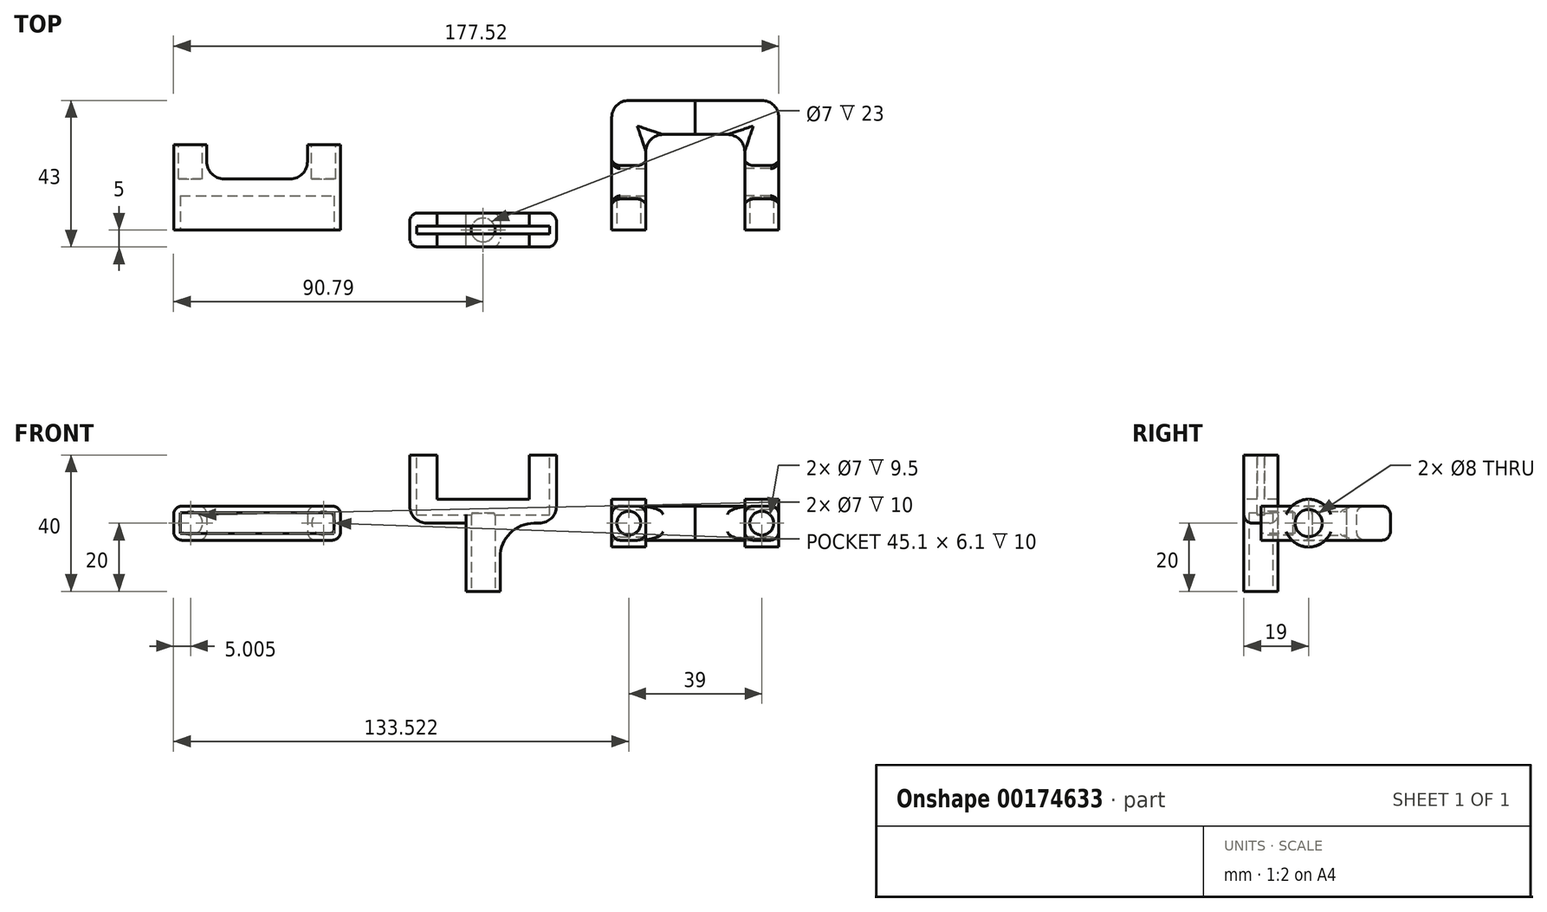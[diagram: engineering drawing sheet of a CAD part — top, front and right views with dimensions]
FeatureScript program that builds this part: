
annotation { "Feature Type Name" : "Feature", "Feature Type Description" : "" }
export const myFeature = defineFeature(function(context is Context, id is Id, definition is map)
    precondition{}
    {
        {
            var Q0;
            Q0=qCreatedBy(makeId("Top.planeOp"),FACE);
            var sketch = newSketch(context, id + "F0", { "sketchPlane" : qUnion([Q0])});
            skLineSegment(sketch, "E0.bottom", {"start": v(21.5, 5) * mm, "end": v(-21.5, 5) * mm});
            skLineSegment(sketch, "E0.top", {"start": v(21.5, -5) * mm, "end": v(-21.5, -5) * mm});
            skLineSegment(sketch, "E0.left", {"start": v(21.5, 5) * mm, "end": v(21.5, -5) * mm});
            skLineSegment(sketch, "E0.right", {"start": v(-21.5, 5) * mm, "end": v(-21.5, -5) * mm});
            skPoint(sketch, "E0.middle", {"position": v(0, 0) * mm});
            skSolve(sketch);
        }
        {
            var Q0;
            Q0=qSketchRegion(id+"F0",true);
            extrude(context, id + "F1", {"entities" : qUnion([Q0]), "depth" : 7 * mm});
        }
        {
            var Q0;
            Q0=makeQuery(id+"F1.opExtrude","CAP_FACE",FACE,{"disambiguationData":[OSD([sQuery(id+"F0.wireOp",EDGE,"E0.bottom"),sQuery(id+"F0.wireOp",EDGE,"E0.top"),sQuery(id+"F0.wireOp",EDGE,"E0.left"),sQuery(id+"F0.wireOp",EDGE,"E0.right")])],"isStart":false});
            var sketch = newSketch(context, id + "F2", { "sketchPlane" : qUnion([Q0])});
            skLineSegment(sketch, "E1.bottom", {"start": v(-21.5, 5) * mm, "end": v(-13.5, 5) * mm});
            skLineSegment(sketch, "E1.top", {"start": v(-21.5, -5) * mm, "end": v(-13.5, -5) * mm});
            skLineSegment(sketch, "E1.left", {"start": v(-21.5, 5) * mm, "end": v(-21.5, -5) * mm});
            skLineSegment(sketch, "E1.right", {"start": v(-13.5, 5) * mm, "end": v(-13.5, -5) * mm});
            skLineSegment(sketch, "E2.bottom", {"start": v(21.5, 5) * mm, "end": v(13.5, 5) * mm});
            skLineSegment(sketch, "E2.top", {"start": v(21.5, -5) * mm, "end": v(13.5, -5) * mm});
            skLineSegment(sketch, "E2.left", {"start": v(21.5, 5) * mm, "end": v(21.5, -5) * mm});
            skLineSegment(sketch, "E2.right", {"start": v(13.5, 5) * mm, "end": v(13.5, -5) * mm});
            skSolve(sketch);
        }
        {
            var Q0;
            Q0=makeQuery(id+"F2.imprint","IMPRINT",FACE,{"disambiguationData":[TD([[makeQuery(id+"F2.imprint","IMPRINT",EDGE,{"derivedFrom":sQuery(id+"F2.wireOp",EDGE,"E1.bottom")}),1.0]])]});
            var Q1;
            Q1=makeQuery(id+"F2.imprint","IMPRINT",FACE,{"disambiguationData":[TD([[makeQuery(id+"F2.imprint","IMPRINT",EDGE,{"derivedFrom":sQuery(id+"F2.wireOp",EDGE,"E2.bottom")}),1.0]])]});
            extrude(context, id + "F3", {"entities" : qUnion([Q0, Q1]), "operationType" : NewBodyOperationType.ADD, "depth" : 13 * mm});
        }
        {
            var Q0;
            Q0=makeQuery(id+"F1.opExtrude","CAP_FACE",FACE,{"disambiguationData":[OSD([sQuery(id+"F0.wireOp",EDGE,"E0.bottom"),sQuery(id+"F0.wireOp",EDGE,"E0.top"),sQuery(id+"F0.wireOp",EDGE,"E0.left"),sQuery(id+"F0.wireOp",EDGE,"E0.right")])],"isStart":true});
            var sketch = newSketch(context, id + "F4", { "sketchPlane" : qUnion([Q0])});
            skLineSegment(sketch, "E3.bottom", {"start": v(-5, 5) * mm, "end": v(5, 5) * mm});
            skLineSegment(sketch, "E3.top", {"start": v(-5, -5) * mm, "end": v(5, -5) * mm});
            skLineSegment(sketch, "E3.left", {"start": v(-5, 5) * mm, "end": v(-5, -5) * mm});
            skLineSegment(sketch, "E3.right", {"start": v(5, 5) * mm, "end": v(5, -5) * mm});
            skPoint(sketch, "E3.middle", {"position": v(0, 0) * mm});
            skSolve(sketch);
        }
        {
            var Q0;
            Q0=makeQuery(id+"F4.imprint","IMPRINT",FACE,{"disambiguationData":[TD([[makeQuery(id+"F4.imprint","IMPRINT",EDGE,{"derivedFrom":sQuery(id+"F4.wireOp",EDGE,"E3.bottom")}),1.0]])]});
            extrude(context, id + "F5", {"entities" : qUnion([Q0]), "operationType" : NewBodyOperationType.ADD, "depth" : 20 * mm});
        }
        {
            var Q0;
            Q0=makeQuery(id+"F5.opExtrude","CAP_FACE",FACE,{"disambiguationData":[OSD([sQuery(id+"F4.wireOp",EDGE,"E3.bottom"),sQuery(id+"F4.wireOp",EDGE,"E3.top"),sQuery(id+"F4.wireOp",EDGE,"E3.left"),sQuery(id+"F4.wireOp",EDGE,"E3.right")])],"isStart":false});
            var sketch = newSketch(context, id + "F6", { "sketchPlane" : qUnion([Q0])});
            skCircle(sketch, "E4", {"center": v(0, 0) * mm, "radius": 3.5 * mm});
            skSolve(sketch);
        }
        {
            var Q0;
            Q0=qSketchRegion(id+"F6",true);
            extrude(context, id + "F7", {"entities" : qUnion([Q0]), "operationType" : NewBodyOperationType.REMOVE, "oppositeDirection" : true, "depth" : 23 * mm});
        }
        {
            var Q0;
            Q0=makeQuery(id+"F5.boolean.opBoolean","MERGE",FACE,{"derivedFrom":[makeQuery(id+"F3.boolean.opBoolean","MERGE",FACE,{"derivedFrom":[makeQuery(id+"F1.opExtrude","SWEPT_FACE",FACE,{"disambiguationData":[OSD([sQuery(id+"F0.wireOp",EDGE,"E0.top")])]}),makeQuery(id+"F3.opExtrude","SWEPT_FACE",FACE,{"disambiguationData":[OSD([sQuery(id+"F2.wireOp",EDGE,"E1.top")])]}),makeQuery(id+"F3.opExtrude","SWEPT_FACE",FACE,{"disambiguationData":[OSD([sQuery(id+"F2.wireOp",EDGE,"E2.top")])]})]}),makeQuery(id+"F5.opExtrude","SWEPT_FACE",FACE,{"disambiguationData":[OSD([sQuery(id+"F4.wireOp",EDGE,"E3.bottom")])]})]});
            var sketch = newSketch(context, id + "F8", { "sketchPlane" : qUnion([Q0])});
            skLineSegment(sketch, "E5", {"start": v(-5, 0) * mm, "end": v(-15, 0) * mm});
            skLineSegment(sketch, "E6", {"start": v(-15, 0) * mm, "end": v(-5, 0) * mm});
            skLineSegment(sketch, "E7", {"start": v(-5, 0) * mm, "end": v(-5, -10) * mm});
            skArc(sketch, "E8", {"start": v(-5, -10) * mm, "mid": v(-7.93, -2.93) * mm, "end": v(-15, 0) * mm});
            skLineSegment(sketch, "E9", {"start": v(5, 0) * mm, "end": v(15, 0) * mm});
            skLineSegment(sketch, "E10", {"start": v(5, 0) * mm, "end": v(5, -10) * mm});
            skArc(sketch, "E11", {"start": v(15, 0) * mm, "mid": v(7.93, -2.93) * mm, "end": v(5, -10) * mm});
            skSolve(sketch);
        }
        {
            var Q0;
            Q0=makeQuery(id+"F8.imprint","IMPRINT",FACE,{"disambiguationData":[TD([[makeQuery(id+"F8.imprint","IMPRINT",EDGE,{"derivedFrom":sQuery(id+"F8.wireOp",EDGE,"E6")}),1.0]])]});
            var Q1;
            Q1=makeQuery(id+"F8.imprint","IMPRINT",FACE,{"disambiguationData":[TD([[makeQuery(id+"F8.imprint","IMPRINT",EDGE,{"derivedFrom":sQuery(id+"F8.wireOp",EDGE,"E9")}),1.0]])]});
            extrude(context, id + "F9", {"entities" : qUnion([Q0, Q1]), "operationType" : NewBodyOperationType.ADD, "oppositeDirection" : true, "depth" : 10 * mm});
        }
        {
            var Q0;
            Q0=makeQuery(id+"F3.opExtrude","CAP_FACE",FACE,{"disambiguationData":[OSD([sQuery(id+"F2.wireOp",EDGE,"E1.bottom"),sQuery(id+"F2.wireOp",EDGE,"E1.top"),sQuery(id+"F2.wireOp",EDGE,"E1.left"),sQuery(id+"F2.wireOp",EDGE,"E1.right")])],"isStart":false});
            var sketch = newSketch(context, id + "F10", { "sketchPlane" : qUnion([Q0])});
            skLineSegment(sketch, "E12.bottom", {"start": v(-19.5, 1.13) * mm, "end": v(19.5, 1.13) * mm});
            skLineSegment(sketch, "E12.top", {"start": v(-19.5, -1.13) * mm, "end": v(19.5, -1.13) * mm});
            skLineSegment(sketch, "E12.left", {"start": v(-19.5, 1.13) * mm, "end": v(-19.5, -1.13) * mm});
            skLineSegment(sketch, "E12.right", {"start": v(19.5, 1.13) * mm, "end": v(19.5, -1.13) * mm});
            skPoint(sketch, "E12.middle", {"position": v(0, 0) * mm});
            skSolve(sketch);
        }
        {
            var Q0;
            Q0=qSketchRegion(id+"F10",true);
            extrude(context, id + "F11", {"entities" : qUnion([Q0]), "oppositeDirection" : true, "depth" : 17.6 * mm});
        }
        {
            var Q0;
            Q0=makeQuery(id+"F11.opExtrude","SWEPT_BODY",BODY,{"disambiguationData":[OSD([sQuery(id+"F10.wireOp",EDGE,"E12.bottom"),sQuery(id+"F10.wireOp",EDGE,"E12.top"),sQuery(id+"F10.wireOp",EDGE,"E12.left"),sQuery(id+"F10.wireOp",EDGE,"E12.right")])]});
            var Q1;
            Q1=makeQuery(id+"F1.opExtrude","SWEPT_BODY",BODY,{"disambiguationData":[OSD([sQuery(id+"F0.wireOp",EDGE,"E0.bottom"),sQuery(id+"F0.wireOp",EDGE,"E0.top"),sQuery(id+"F0.wireOp",EDGE,"E0.left"),sQuery(id+"F0.wireOp",EDGE,"E0.right")])]});
            booleanBodies(context, id + "F12", {"operationType" : BooleanOperationType.SUBTRACTION, "tools" : qUnion([Q0]), "targets" : qUnion([Q1])});
        }
        {
            var Q0;
            Q0=makeQuery(id+"F1.opExtrude","CAP_EDGE",EDGE,{"disambiguationData":[OSD([sQuery(id+"F0.wireOp",EDGE,"E0.right")])],"isStart":true});
            fillet(context, id + "F13", {"entities" : qUnion([Q0]), "radius" : 5 * mm, "tangentPropagation" : true, "allowEdgeOverflow" : false});
        }
        {
            var Q0;
            Q0=makeQuery(id+"F1.opExtrude","CAP_EDGE",EDGE,{"disambiguationData":[OSD([sQuery(id+"F0.wireOp",EDGE,"E0.left")])],"isStart":true});
            fillet(context, id + "F14", {"entities" : qUnion([Q0]), "radius" : 5 * mm, "tangentPropagation" : true, "allowEdgeOverflow" : false});
        }
        {
            var Q0;
            Q0=makeQuery(id+"F3.boolean.opBoolean","MERGE",EDGE,{"derivedFrom":[makeQuery(id+"F1.opExtrude","SWEPT_EDGE",EDGE,{"disambiguationData":[OSD([sQuery(id+"F0.wireOp",EDGE,"E0.bottom"),sQuery(id+"F0.wireOp",EDGE,"E0.right")])]}),makeQuery(id+"F3.opExtrude","SWEPT_EDGE",EDGE,{"disambiguationData":[OSD([sQuery(id+"F2.wireOp",EDGE,"E1.bottom"),sQuery(id+"F2.wireOp",EDGE,"E1.left")])]})]});
            var Q1;
            Q1=makeQuery(id+"F3.boolean.opBoolean","MERGE",EDGE,{"derivedFrom":[makeQuery(id+"F1.opExtrude","SWEPT_EDGE",EDGE,{"disambiguationData":[OSD([sQuery(id+"F0.wireOp",EDGE,"E0.top"),sQuery(id+"F0.wireOp",EDGE,"E0.right")])]}),makeQuery(id+"F3.opExtrude","SWEPT_EDGE",EDGE,{"disambiguationData":[OSD([sQuery(id+"F2.wireOp",EDGE,"E1.top"),sQuery(id+"F2.wireOp",EDGE,"E1.left")])]})]});
            var Q2;
            Q2=makeQuery(id+"F9.opExtrude","CAP_EDGE",EDGE,{"disambiguationData":[OSD([sQuery(id+"F8.wireOp",EDGE,"E11")])],"isStart":false});
            var Q3;
            Q3=makeQuery(id+"F3.boolean.opBoolean","MERGE",EDGE,{"derivedFrom":[makeQuery(id+"F1.opExtrude","SWEPT_EDGE",EDGE,{"disambiguationData":[OSD([sQuery(id+"F0.wireOp",EDGE,"E0.top"),sQuery(id+"F0.wireOp",EDGE,"E0.left")])]}),makeQuery(id+"F3.opExtrude","SWEPT_EDGE",EDGE,{"disambiguationData":[OSD([sQuery(id+"F2.wireOp",EDGE,"E2.top"),sQuery(id+"F2.wireOp",EDGE,"E2.left")])]})]});
            var Q4;
            {var subQ0=sQuery(id+"F2.wireOp",EDGE,"E1.right");var subQ1=sQuery(id+"F0.wireOp",EDGE,"E0.bottom");Q4=makeQuery(id+"F12.opBoolean","SPLIT",EDGE,{"disambiguationData":[TD([makeQuery(id+"F1.opExtrude","SWEPT_FACE",FACE,{"disambiguationData":[OSD([subQ1])]})])],"derivedFrom":makeQuery(id+"F3.opExtrude","CAP_EDGE",EDGE,{"disambiguationData":[OSD([subQ0])],"isStart":true})});}
            var Q5;
            {var subQ0=sQuery(id+"F2.wireOp",EDGE,"E1.right");var subQ1=sQuery(id+"F0.wireOp",EDGE,"E0.top");Q5=makeQuery(id+"F12.opBoolean","SPLIT",EDGE,{"disambiguationData":[TD([makeQuery(id+"F1.opExtrude","SWEPT_FACE",FACE,{"disambiguationData":[OSD([subQ1])]})])],"derivedFrom":makeQuery(id+"F3.opExtrude","CAP_EDGE",EDGE,{"disambiguationData":[OSD([subQ0])],"isStart":true})});}
            var Q6;
            {var subQ0=sQuery(id+"F0.wireOp",EDGE,"E0.bottom");var subQ1=sQuery(id+"F2.wireOp",EDGE,"E2.right");Q6=makeQuery(id+"F12.opBoolean","SPLIT",EDGE,{"disambiguationData":[TD([makeQuery(id+"F1.opExtrude","SWEPT_FACE",FACE,{"disambiguationData":[OSD([subQ0])]})])],"derivedFrom":makeQuery(id+"F3.opExtrude","CAP_EDGE",EDGE,{"disambiguationData":[OSD([subQ1])],"isStart":true})});}
            var Q7;
            {var subQ0=sQuery(id+"F0.wireOp",EDGE,"E0.top");var subQ1=sQuery(id+"F2.wireOp",EDGE,"E2.right");Q7=makeQuery(id+"F12.opBoolean","SPLIT",EDGE,{"disambiguationData":[TD([makeQuery(id+"F1.opExtrude","SWEPT_FACE",FACE,{"disambiguationData":[OSD([subQ0])]})])],"derivedFrom":makeQuery(id+"F3.opExtrude","CAP_EDGE",EDGE,{"disambiguationData":[OSD([subQ1])],"isStart":true})});}
            fillet(context, id + "F15", {"entities" : qUnion([Q0, Q1, Q2, Q3, Q4, Q5, Q6, Q7]), "radius" : 2.5 * mm, "tangentPropagation" : true, "allowEdgeOverflow" : false});
        }
        {
            var Q0;
            Q0=qCreatedBy(makeId("Front.planeOp"),FACE);
            var sketch = newSketch(context, id + "F16", { "sketchPlane" : qUnion([Q0])});
            skLineSegment(sketch, "E13.bottom", {"start": v(-90.79, 5) * mm, "end": v(-41.79, 5) * mm});
            skLineSegment(sketch, "E13.top", {"start": v(-90.79, -5) * mm, "end": v(-41.79, -5) * mm});
            skLineSegment(sketch, "E13.left", {"start": v(-90.79, 5) * mm, "end": v(-90.79, -5) * mm});
            skLineSegment(sketch, "E13.right", {"start": v(-41.79, 5) * mm, "end": v(-41.79, -5) * mm});
            skPoint(sketch, "E14", {"position": v(-66.29, 0) * mm});
            skSolve(sketch);
        }
        {
            var Q0;
            Q0=qSketchRegion(id+"F16",true);
            extrude(context, id + "F17", {"entities" : qUnion([Q0]), "oppositeDirection" : true, "depth" : 25 * mm});
        }
        {
            var Q0;
            Q0=makeQuery(id+"F17.opExtrude","CAP_FACE",FACE,{"disambiguationData":[OSD([sQuery(id+"F16.wireOp",EDGE,"E13.bottom"),sQuery(id+"F16.wireOp",EDGE,"E13.top"),sQuery(id+"F16.wireOp",EDGE,"E13.left"),sQuery(id+"F16.wireOp",EDGE,"E13.right")])],"isStart":true});
            var sketch = newSketch(context, id + "F18", { "sketchPlane" : qUnion([Q0])});
            skLineSegment(sketch, "E15", {"start": v(-66.29, 5) * mm, "end": v(-66.29, -5) * mm, "construction": true});
            skLineSegment(sketch, "E16.bottom", {"start": v(-88.84, 3.05) * mm, "end": v(-43.74, 3.05) * mm});
            skLineSegment(sketch, "E16.top", {"start": v(-88.84, -3.05) * mm, "end": v(-43.74, -3.05) * mm});
            skLineSegment(sketch, "E16.left", {"start": v(-88.84, 3.05) * mm, "end": v(-88.84, -3.05) * mm});
            skLineSegment(sketch, "E16.right", {"start": v(-43.74, 3.05) * mm, "end": v(-43.74, -3.05) * mm});
            skPoint(sketch, "E16.middle", {"position": v(-66.29, 0) * mm});
            skSolve(sketch);
        }
        {
            var Q0;
            Q0=qSketchRegion(id+"F18",true);
            extrude(context, id + "F19", {"entities" : qUnion([Q0]), "operationType" : NewBodyOperationType.REMOVE, "oppositeDirection" : true, "depth" : 10 * mm});
        }
        {
            var Q0;
            Q0=makeQuery(id+"F17.opExtrude","CAP_FACE",FACE,{"disambiguationData":[OSD([sQuery(id+"F16.wireOp",EDGE,"E13.bottom"),sQuery(id+"F16.wireOp",EDGE,"E13.top"),sQuery(id+"F16.wireOp",EDGE,"E13.left"),sQuery(id+"F16.wireOp",EDGE,"E13.right")])],"isStart":false});
            var sketch = newSketch(context, id + "F20", { "sketchPlane" : qUnion([Q0])});
            skLineSegment(sketch, "E17", {"start": v(41.79, 0) * mm, "end": v(90.79, 0) * mm, "construction": true});
            skLineSegment(sketch, "E18", {"start": v(41.79, 0) * mm, "end": v(46.79, 0) * mm, "construction": true});
            skPoint(sketch, "E19.middle", {"position": v(46.79, 0) * mm});
            skLineSegment(sketch, "E20", {"start": v(90.79, 0) * mm, "end": v(85.79, 0) * mm, "construction": true});
            skPoint(sketch, "E21.middle", {"position": v(85.79, 0) * mm});
            skCircle(sketch, "E22", {"center": v(85.79, 0) * mm, "radius": 3.5 * mm});
            skCircle(sketch, "E23", {"center": v(46.79, 0) * mm, "radius": 3.5 * mm});
            skSolve(sketch);
        }
        {
            var Q0;
            Q0=qSketchRegion(id+"F20",true);
            extrude(context, id + "F21", {"entities" : qUnion([Q0]), "operationType" : NewBodyOperationType.REMOVE, "oppositeDirection" : true, "depth" : 10 * mm});
        }
        {
            var Q0;
            Q0=makeQuery(id+"F17.opExtrude","SWEPT_EDGE",EDGE,{"disambiguationData":[OSD([sQuery(id+"F16.wireOp",EDGE,"E13.bottom"),sQuery(id+"F16.wireOp",EDGE,"E13.left")])]});
            var Q1;
            Q1=makeQuery(id+"F17.opExtrude","SWEPT_EDGE",EDGE,{"disambiguationData":[OSD([sQuery(id+"F16.wireOp",EDGE,"E13.bottom"),sQuery(id+"F16.wireOp",EDGE,"E13.right")])]});
            var Q2;
            Q2=makeQuery(id+"F17.opExtrude","SWEPT_EDGE",EDGE,{"disambiguationData":[OSD([sQuery(id+"F16.wireOp",EDGE,"E13.top"),sQuery(id+"F16.wireOp",EDGE,"E13.right")])]});
            var Q3;
            Q3=makeQuery(id+"F17.opExtrude","SWEPT_EDGE",EDGE,{"disambiguationData":[OSD([sQuery(id+"F16.wireOp",EDGE,"E13.top"),sQuery(id+"F16.wireOp",EDGE,"E13.left")])]});
            fillet(context, id + "F22", {"entities" : qUnion([Q0, Q1, Q2, Q3]), "radius" : 2.5 * mm, "tangentPropagation" : true, "allowEdgeOverflow" : false});
        }
        {
            var Q0;
            Q0=makeQuery(id+"F17.opExtrude","CAP_FACE",FACE,{"disambiguationData":[OSD([sQuery(id+"F16.wireOp",EDGE,"E13.bottom"),sQuery(id+"F16.wireOp",EDGE,"E13.top"),sQuery(id+"F16.wireOp",EDGE,"E13.left"),sQuery(id+"F16.wireOp",EDGE,"E13.right")])],"isStart":false});
            var sketch = newSketch(context, id + "F23", { "sketchPlane" : qUnion([Q0])});
            skLineSegment(sketch, "E24", {"start": v(41.79, 0) * mm, "end": v(90.79, 0) * mm, "construction": true});
            skLineSegment(sketch, "E25.bottom", {"start": v(51.54, 7.07) * mm, "end": v(81.04, 7.07) * mm});
            skLineSegment(sketch, "E25.top", {"start": v(51.54, -7.07) * mm, "end": v(81.04, -7.07) * mm});
            skLineSegment(sketch, "E25.left", {"start": v(51.54, 7.07) * mm, "end": v(51.54, -7.07) * mm});
            skLineSegment(sketch, "E25.right", {"start": v(81.04, 7.07) * mm, "end": v(81.04, -7.07) * mm});
            skPoint(sketch, "E25.middle", {"position": v(66.29, 0) * mm});
            skSolve(sketch);
        }
        {
            var Q0;
            Q0=qSketchRegion(id+"F23",true);
            extrude(context, id + "F24", {"entities" : qUnion([Q0]), "operationType" : NewBodyOperationType.REMOVE, "oppositeDirection" : true, "depth" : 10 * mm});
        }
        {
            var Q0;
            Q0=makeQuery(id+"F24.boolean.opBoolean","COPY",EDGE,{"derivedFrom":makeQuery(id+"F24.opExtrude","CAP_EDGE",EDGE,{"disambiguationData":[OSD([sQuery(id+"F23.wireOp",EDGE,"E25.left")])],"isStart":false})});
            var Q1;
            Q1=makeQuery(id+"F24.boolean.opBoolean","COPY",EDGE,{"derivedFrom":makeQuery(id+"F24.opExtrude","CAP_EDGE",EDGE,{"disambiguationData":[OSD([sQuery(id+"F23.wireOp",EDGE,"E25.right")])],"isStart":false})});
            fillet(context, id + "F25", {"entities" : qUnion([Q0, Q1]), "radius" : 5 * mm, "tangentPropagation" : true, "allowEdgeOverflow" : false});
        }
        {
            var Q0;
            Q0=makeQuery(id+"F24.boolean.opBoolean","INTERSECT",EDGE,{"derivedFrom":[makeQuery(id+"F17.opExtrude","SWEPT_FACE",FACE,{"disambiguationData":[OSD([sQuery(id+"F16.wireOp",EDGE,"E13.bottom")])]}),makeQuery(id+"F24.opExtrude","SWEPT_FACE",FACE,{"disambiguationData":[OSD([sQuery(id+"F23.wireOp",EDGE,"E25.left")])]})]});
            var Q1;
            Q1=makeQuery(id+"F24.boolean.opBoolean","INTERSECT",EDGE,{"derivedFrom":[makeQuery(id+"F17.opExtrude","SWEPT_FACE",FACE,{"disambiguationData":[OSD([sQuery(id+"F16.wireOp",EDGE,"E13.top")])]}),makeQuery(id+"F24.opExtrude","CAP_FACE",FACE,{"disambiguationData":[OSD([sQuery(id+"F23.wireOp",EDGE,"E25.bottom"),sQuery(id+"F23.wireOp",EDGE,"E25.top"),sQuery(id+"F23.wireOp",EDGE,"E25.left"),sQuery(id+"F23.wireOp",EDGE,"E25.right")])],"isStart":false})]});
            fillet(context, id + "F26", {"entities" : qUnion([Q0, Q1]), "radius" : 2.5 * mm, "tangentPropagation" : true, "allowEdgeOverflow" : false});
        }
        {
            var Q0;
            Q0=qCreatedBy(makeId("Top.planeOp"),FACE);
            var sketch = newSketch(context, id + "F27", { "sketchPlane" : qUnion([Q0])});
            skLineSegment(sketch, "E26.bottom", {"start": v(37.73, 0) * mm, "end": v(47.73, 0) * mm});
            skLineSegment(sketch, "E26.top", {"start": v(37.73, 38) * mm, "end": v(62.23, 38) * mm});
            skLineSegment(sketch, "E26.left", {"start": v(37.73, 0) * mm, "end": v(37.73, 38) * mm});
            skLineSegment(sketch, "E26.right", {"start": v(62.23, 28) * mm, "end": v(62.23, 38) * mm});
            skLineSegment(sketch, "E27.top", {"start": v(62.23, 28) * mm, "end": v(47.73, 28) * mm});
            skLineSegment(sketch, "E27.right", {"start": v(47.73, 0) * mm, "end": v(47.73, 28) * mm});
            skPoint(sketch, "E28.orphan", {"position": v(62.23, 0) * mm});
            skLineSegment(sketch, "E29", {"start": v(62.23, 0) * mm, "end": v(62.23, 45.65) * mm, "construction": true});
            skLineSegment(sketch, "E30", {"start": v(32.97, 14) * mm, "end": v(53.85, 14) * mm, "construction": true});
            skLineSegment(sketch, "E31", {"start": v(35.58, 10) * mm, "end": v(51.63, 10) * mm, "construction": true});
            skLineSegment(sketch, "E32", {"start": v(35.58, 18) * mm, "end": v(51.63, 18) * mm, "construction": true});
            skSolve(sketch);
        }
        {
            var Q0;
            Q0=qSketchRegion(id+"F27",true);
            extrude(context, id + "F28", {"entities" : qUnion([Q0]), "depth" : 5 * mm, "hasSecondDirection" : true, "secondDirectionOppositeDirection" : true, "secondDirectionDepth" : 5 * mm});
        }
        {
            var Q0;
            Q0=makeQuery(id+"F28.opExtrude","SWEPT_FACE",FACE,{"disambiguationData":[OSD([sQuery(id+"F27.wireOp",EDGE,"E27.right")])]});
            var sketch = newSketch(context, id + "F29", { "sketchPlane" : qUnion([Q0])});
            skLineSegment(sketch, "E33", {"start": v(0, 0) * mm, "end": v(14, 0) * mm, "construction": true});
            skCircle(sketch, "E34", {"center": v(14, 0) * mm, "radius": 7 * mm});
            skSolve(sketch);
        }
        {
            var Q0;
            Q0=qSketchRegion(id+"F29",true);
            extrude(context, id + "F30", {"entities" : qUnion([Q0]), "operationType" : NewBodyOperationType.ADD, "oppositeDirection" : true, "depth" : 10 * mm});
        }
        {
            var Q0;
            Q0=makeQuery(id+"F28.opExtrude","SWEPT_FACE",FACE,{"disambiguationData":[OSD([sQuery(id+"F27.wireOp",EDGE,"E27.right")])]});
            var sketch = newSketch(context, id + "F31", { "sketchPlane" : qUnion([Q0])});
            skLineSegment(sketch, "E35", {"start": v(0, 0) * mm, "end": v(14, 0) * mm, "construction": true});
            skPoint(sketch, "E35.endSnap0", {"position": v(0, 0) * mm});
            skCircle(sketch, "E36", {"center": v(14, 0) * mm, "radius": 4 * mm});
            skSolve(sketch);
        }
        {
            var Q0;
            Q0=qSketchRegion(id+"F31",true);
            extrude(context, id + "F32", {"entities" : qUnion([Q0]), "operationType" : NewBodyOperationType.REMOVE, "oppositeDirection" : true, "depth" : 17.3 * mm});
        }
        {
            var Q0;
            Q0=makeQuery(id+"F28.opExtrude","SWEPT_FACE",FACE,{"disambiguationData":[OSD([sQuery(id+"F27.wireOp",EDGE,"E26.bottom")])]});
            var sketch = newSketch(context, id + "F33", { "sketchPlane" : qUnion([Q0])});
            skLineSegment(sketch, "E37", {"start": v(37.73, 0) * mm, "end": v(47.73, 0) * mm, "construction": true});
            skPoint(sketch, "E38.middle", {"position": v(42.73, 0) * mm});
            skCircle(sketch, "E39", {"center": v(42.73, 0) * mm, "radius": 3.5 * mm});
            skSolve(sketch);
        }
        {
            var Q0;
            Q0=qSketchRegion(id+"F33",true);
            extrude(context, id + "F34", {"entities" : qUnion([Q0]), "operationType" : NewBodyOperationType.REMOVE, "oppositeDirection" : true, "depth" : 9.5 * mm});
        }
        {
            var Q0;
            Q0=makeQuery(id+"F32.boolean.opBoolean","COPY",EDGE,{"derivedFrom":makeQuery(id+"F32.opExtrude","CAP_EDGE",EDGE,{"disambiguationData":[OSD([sQuery(id+"F31.wireOp",EDGE,"E36")])],"isStart":true})});
            var Q1;
            Q1=makeQuery(id+"F32.boolean.opBoolean","INTERSECT",EDGE,{"derivedFrom":[makeQuery(id+"F30.boolean.opBoolean","MERGE",FACE,{"derivedFrom":[makeQuery(id+"F28.opExtrude","SWEPT_FACE",FACE,{"disambiguationData":[OSD([sQuery(id+"F27.wireOp",EDGE,"E26.left")])]}),makeQuery(id+"F30.opExtrude","CAP_FACE",FACE,{"disambiguationData":[OSD([sQuery(id+"F29.wireOp",EDGE,"E34")])],"isStart":false})]}),makeQuery(id+"F32.opExtrude","SWEPT_FACE",FACE,{"disambiguationData":[OSD([sQuery(id+"F31.wireOp",EDGE,"E36")])]})]});
            var Q2;
            {var subQ0=sQuery(id+"F27.wireOp",EDGE,"E27.right");var subQ2=sQuery(id+"F27.wireOp",EDGE,"E26.bottom");Q2=makeQuery(id+"F30.boolean.opBoolean","SPLIT",EDGE,{"disambiguationData":[TD([makeQuery(id+"F28.opExtrude","SWEPT_FACE",FACE,{"disambiguationData":[OSD([subQ2])]})])],"derivedFrom":makeQuery(id+"F28.opExtrude","CAP_EDGE",EDGE,{"disambiguationData":[OSD([subQ0])],"isStart":false})});}
            var Q3;
            {var subQ0=sQuery(id+"F27.wireOp",EDGE,"E27.right");var subQ2=sQuery(id+"F27.wireOp",EDGE,"E26.bottom");Q3=makeQuery(id+"F30.boolean.opBoolean","SPLIT",EDGE,{"disambiguationData":[TD([makeQuery(id+"F28.opExtrude","SWEPT_FACE",FACE,{"disambiguationData":[OSD([subQ2])]})])],"derivedFrom":makeQuery(id+"F28.opExtrude","CAP_EDGE",EDGE,{"disambiguationData":[OSD([subQ0])],"isStart":true})});}
            var Q4;
            {var subQ0=sQuery(id+"F27.wireOp",EDGE,"E27.right");var subQ1=sQuery(id+"F27.wireOp",EDGE,"E27.top");Q4=makeQuery(id+"F30.boolean.opBoolean","SPLIT",EDGE,{"disambiguationData":[TD([makeQuery(id+"F28.opExtrude","SWEPT_FACE",FACE,{"disambiguationData":[OSD([subQ1])]})])],"derivedFrom":makeQuery(id+"F28.opExtrude","CAP_EDGE",EDGE,{"disambiguationData":[OSD([subQ0])],"isStart":false})});}
            var Q5;
            {var subQ0=sQuery(id+"F27.wireOp",EDGE,"E27.right");var subQ1=sQuery(id+"F27.wireOp",EDGE,"E27.top");Q5=makeQuery(id+"F30.boolean.opBoolean","SPLIT",EDGE,{"disambiguationData":[TD([makeQuery(id+"F28.opExtrude","SWEPT_FACE",FACE,{"disambiguationData":[OSD([subQ1])]})])],"derivedFrom":makeQuery(id+"F28.opExtrude","CAP_EDGE",EDGE,{"disambiguationData":[OSD([subQ0])],"isStart":true})});}
            var Q6;
            {var subQ0=sQuery(id+"F27.wireOp",EDGE,"E26.left");var subQ2=sQuery(id+"F27.wireOp",EDGE,"E26.bottom");Q6=makeQuery(id+"F30.boolean.opBoolean","SPLIT",EDGE,{"disambiguationData":[TD([makeQuery(id+"F28.opExtrude","SWEPT_FACE",FACE,{"disambiguationData":[OSD([subQ2])]})])],"derivedFrom":makeQuery(id+"F28.opExtrude","CAP_EDGE",EDGE,{"disambiguationData":[OSD([subQ0])],"isStart":false})});}
            var Q7;
            {var subQ0=sQuery(id+"F27.wireOp",EDGE,"E26.left");var subQ2=sQuery(id+"F27.wireOp",EDGE,"E26.top");Q7=makeQuery(id+"F30.boolean.opBoolean","SPLIT",EDGE,{"disambiguationData":[TD([makeQuery(id+"F28.opExtrude","SWEPT_FACE",FACE,{"disambiguationData":[OSD([subQ2])]})])],"derivedFrom":makeQuery(id+"F28.opExtrude","CAP_EDGE",EDGE,{"disambiguationData":[OSD([subQ0])],"isStart":false})});}
            var Q8;
            Q8=makeQuery(id+"F28.opExtrude","CAP_EDGE",EDGE,{"disambiguationData":[OSD([sQuery(id+"F27.wireOp",EDGE,"E27.top")])],"isStart":false});
            var Q9;
            Q9=makeQuery(id+"F28.opExtrude","CAP_EDGE",EDGE,{"disambiguationData":[OSD([sQuery(id+"F27.wireOp",EDGE,"E27.top")])],"isStart":true});
            var Q10;
            Q10=makeQuery(id+"F28.opExtrude","CAP_EDGE",EDGE,{"disambiguationData":[OSD([sQuery(id+"F27.wireOp",EDGE,"E26.top")])],"isStart":false});
            var Q11;
            Q11=makeQuery(id+"F28.opExtrude","CAP_EDGE",EDGE,{"disambiguationData":[OSD([sQuery(id+"F27.wireOp",EDGE,"E26.top")])],"isStart":true});
            var Q12;
            {var subQ0=sQuery(id+"F27.wireOp",EDGE,"E26.left");var subQ2=sQuery(id+"F27.wireOp",EDGE,"E26.top");Q12=makeQuery(id+"F30.boolean.opBoolean","SPLIT",EDGE,{"disambiguationData":[TD([makeQuery(id+"F28.opExtrude","SWEPT_FACE",FACE,{"disambiguationData":[OSD([subQ2])]})])],"derivedFrom":makeQuery(id+"F28.opExtrude","CAP_EDGE",EDGE,{"disambiguationData":[OSD([subQ0])],"isStart":true})});}
            var Q13;
            {var subQ0=sQuery(id+"F27.wireOp",EDGE,"E26.left");var subQ2=sQuery(id+"F27.wireOp",EDGE,"E26.bottom");Q13=makeQuery(id+"F30.boolean.opBoolean","SPLIT",EDGE,{"disambiguationData":[TD([makeQuery(id+"F28.opExtrude","SWEPT_FACE",FACE,{"disambiguationData":[OSD([subQ2])]})])],"derivedFrom":makeQuery(id+"F28.opExtrude","CAP_EDGE",EDGE,{"disambiguationData":[OSD([subQ0])],"isStart":true})});}
            fillet(context, id + "F35", {"entities" : qUnion([Q0, Q1, Q2, Q3, Q4, Q5, Q6, Q7, Q8, Q9, Q10, Q11, Q12, Q13]), "radius" : 2.5 * mm, "tangentPropagation" : true, "allowEdgeOverflow" : false});
        }
        {
            var Q0;
            Q0=makeQuery(id+"F28.opExtrude","SWEPT_EDGE",EDGE,{"disambiguationData":[OSD([sQuery(id+"F27.wireOp",EDGE,"E27.top"),sQuery(id+"F27.wireOp",EDGE,"E27.right")])]});
            var Q1;
            Q1=makeQuery(id+"F28.opExtrude","SWEPT_EDGE",EDGE,{"disambiguationData":[OSD([sQuery(id+"F27.wireOp",EDGE,"E26.top"),sQuery(id+"F27.wireOp",EDGE,"E26.left")])]});
            fillet(context, id + "F36", {"entities" : qUnion([Q0, Q1]), "radius" : 5 * mm, "tangentPropagation" : true, "allowEdgeOverflow" : false});
        }
        {
            var Q0;
            Q0=makeQuery(id+"F28.opExtrude","SWEPT_BODY",BODY,{"disambiguationData":[OSD([sQuery(id+"F27.wireOp",EDGE,"E26.bottom"),sQuery(id+"F27.wireOp",EDGE,"E26.top"),sQuery(id+"F27.wireOp",EDGE,"E26.left"),sQuery(id+"F27.wireOp",EDGE,"E26.right"),sQuery(id+"F27.wireOp",EDGE,"E27.top"),sQuery(id+"F27.wireOp",EDGE,"E27.right")])]});
            var Q1;
            Q1=makeQuery(id+"F28.opExtrude","SWEPT_FACE",FACE,{"disambiguationData":[OSD([sQuery(id+"F27.wireOp",EDGE,"E26.right")])]});
            mirror(context, id + "F37", {"operationType" : NewBodyOperationType.ADD, "entities" : qUnion([Q0]), "mirrorPlane" : qUnion([Q1])});
        }
    });
